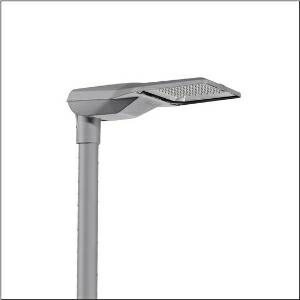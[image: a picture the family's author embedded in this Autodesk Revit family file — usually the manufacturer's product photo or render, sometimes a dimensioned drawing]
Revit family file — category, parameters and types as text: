
# Revit family: streetlight_sl_21_iq_midi___stw1_0a_5xe3e41g08nb_77a4
name_source: partatom
category: Lighting Fixtures
units: mm (PartAtom-declared; Revit-internal decimal feet)

## family parameters
Cut with Voids When Loaded = No
Host = Face
Light Source = No
Part Type = Normal
Room Calculation Point = No
Round Connector Dimension = Use Diameter
Shared = No

## types (1)
- --- (1 x LED, 24250 lm, 155.5 W, 4000K)
    Apparent Load = 155 VA
    CIE Flux Codes = 39 75 98 100 100
    Color Rendering = 70
    Color Temperature = 4000K
    Default Elevation = 1800 mm
    Description = Streetlight SL 21 iQ midi, mast luminaire, primary light control with lens, of PMMA, primary optical cover: cover, of toughened safety glass, transparent, light distribution: STW1.0a, light emission: direct distribution, primary light characteristic: asymmetric, installation type: post-top, side-entry, LED, High Power LED, rated luminous flux: 24.250lm, luminous efficacy: 156lm/W, light colour: 740, colour temperature: 4000K, control gear: iQ Street-Remote, control: Street-Remote, Auto-Match, Temp-Guard, Lumen-Switch, Night-Set, Smart-Wire, Light-Fading, Desk-Remote (wireless, voltage-free reading and setting of iQ features in the workshop via application-optimized NFC function/RFID function), optimised constant luminous flux control (CLO 2.0), pre-setting: linear dimming characteristic, mains connection: 230..240V, AC, 50/60Hz, start of lifetime: 156W, end of service life: 162W, reduction: 69W, luminaire housing, of diecast aluminium, powder-coated, Siteco® metallic grey (DB 702S), corrosivity category C5 mid according to DIN EN ISO 12944, please order mast flange separately, inclination adjustable: 0°, 5°, 10°, 15°, sealing non-destructively replaceable, multi-level sealing system, length: 644mm, width: 335mm, height: 110mm, mast flange for spigot size: 42mm (side-entry): 5XC10008XM4, 60/48mm (side-entry/post-top): 5XC10108XM2, 76/60mm (side-entry/post-top): 5XC10108XM1, mounting height: 4..8m, protection rating (complete): IP66, insulation class (complete): insulation class II (safety insulation), certification: CE, ENEC, ENEC+, VDE, impact resistance: IK10, permissible operating ambient temperature for outdoor applications: -40..+50°C, standard-compliant lighting for roads and squares, packaging unit: 1 piece

Light Distribution: STW1.0a
    Height = 111 mm
    Lamp = 1 x LED
    Lamp Light Flux = 24250 lm
    Lamp Power = 155.5 W
    Lamp count = 1
    Length = 644 mm
    Luminous efficacy = 156 lm/W
    Manufacturer = Siteco
    ModVariant = No
    Model = 5XE3E41G08NB
    Number of Poles = 1
    OnlyDefault = Yes
    Power Factor = 1
    Product Name = Streetlight SL 21 iQ midi | STW1.0a
    Product group = mast luminaire | pylon top
    ProductGroupID = 6100
    Protection Class = Protection class II
    Protection Degree = IP 66
    RLX_Detail_Level = 1
    RLX_Emergency_Light_Flux = 0 lm
    RLX_Emergency_Type = 0
    RLX_Emergency_Type_DB = No
    RlxData = <blob elided: 27269 chars, md5=90a823ab>
    Socket = socket
    Standby Power = 0 W
    System Light Flux = 24250 lm
    System Power = 155 W
    Type Comments = factory setting: luminous flux: 100 % | dim-lin: 254 | 823 mA
    Type Image = l_1004298.jpg
    URL = http://relux.com
    VarID = @adj_191269
    Voltage = 0 V
    Weight = 0.00 kg
    Width = 336 mm

## geometry (parser evidence)
native form markers: Blend x4, Sweep x12
no freeform markers — native parametric forms only
